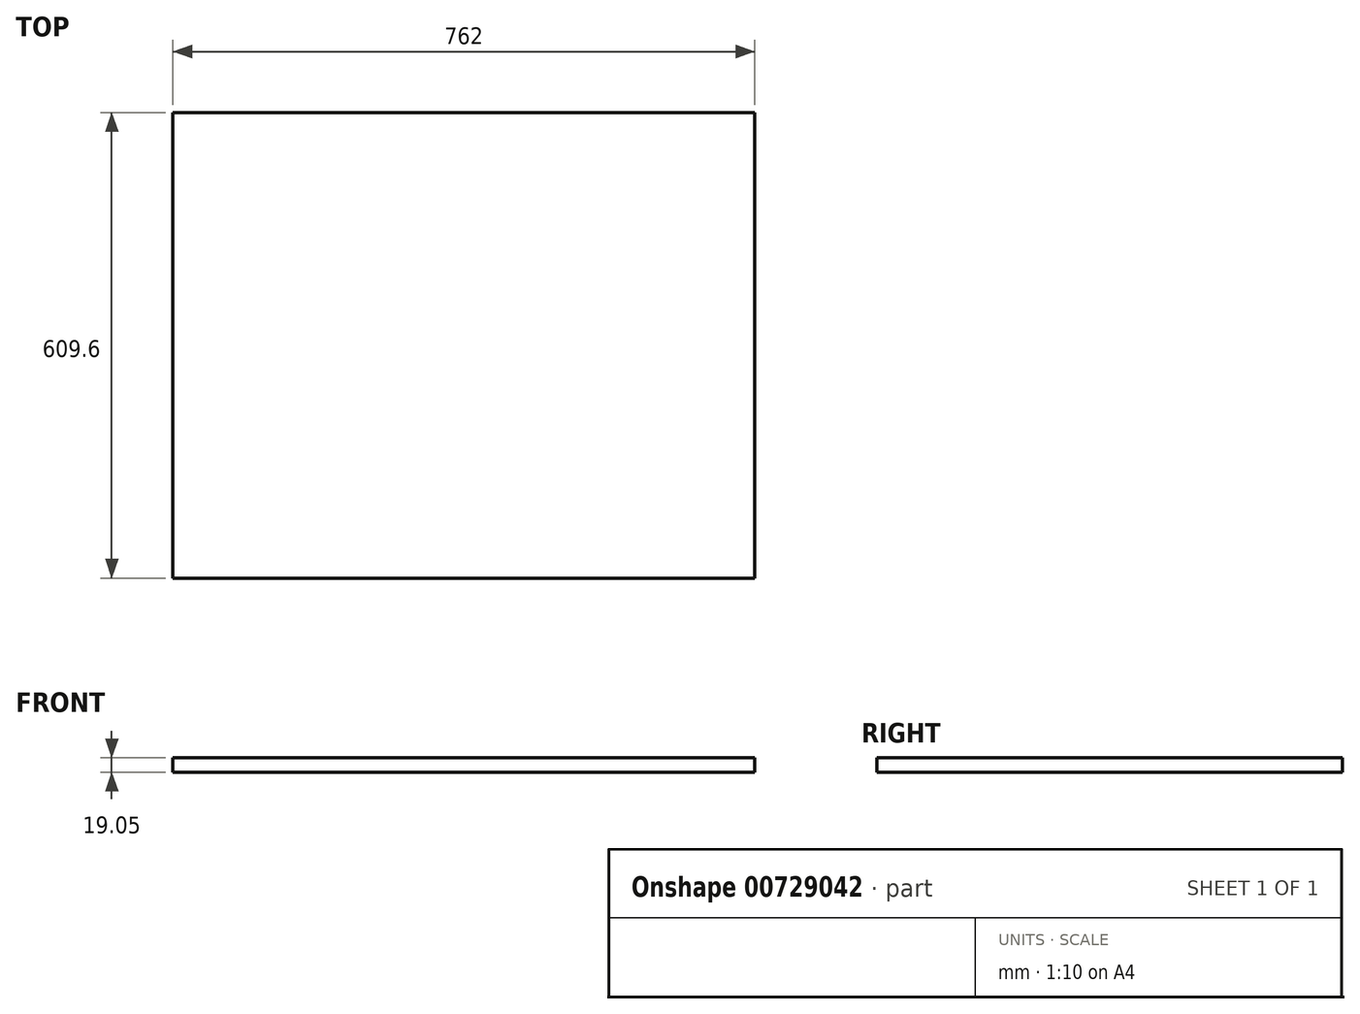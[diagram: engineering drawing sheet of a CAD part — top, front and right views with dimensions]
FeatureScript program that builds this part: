
annotation { "Feature Type Name" : "Feature", "Feature Type Description" : "" }
export const myFeature = defineFeature(function(context is Context, id is Id, definition is map)
    precondition{}
    {
        {
            var Q0;
            Q0=qCreatedBy(makeId("Top.planeOp"),FACE);
            var sketch = newSketch(context, id + "F0", { "sketchPlane" : qUnion([Q0])});
            skLineSegment(sketch, "E0.bottom", {"start": v(381, -304.8) * mm, "end": v(-381, -304.8) * mm});
            skLineSegment(sketch, "E0.top", {"start": v(381, 304.8) * mm, "end": v(-381, 304.8) * mm});
            skLineSegment(sketch, "E0.left", {"start": v(381, -304.8) * mm, "end": v(381, 304.8) * mm});
            skLineSegment(sketch, "E0.right", {"start": v(-381, -304.8) * mm, "end": v(-381, 304.8) * mm});
            skPoint(sketch, "E0.middle", {"position": v(0, 0) * mm});
            skSolve(sketch);
        }
        {
            var Q0;
            Q0 = qSketchRegion(id + "F0", true);
            extrude(context, id + "F1", {"entities" : qUnion([Q0]), "depth" : 19.05 * mm, "offsetDistance" : 25.4 * mm});
        }
    });
